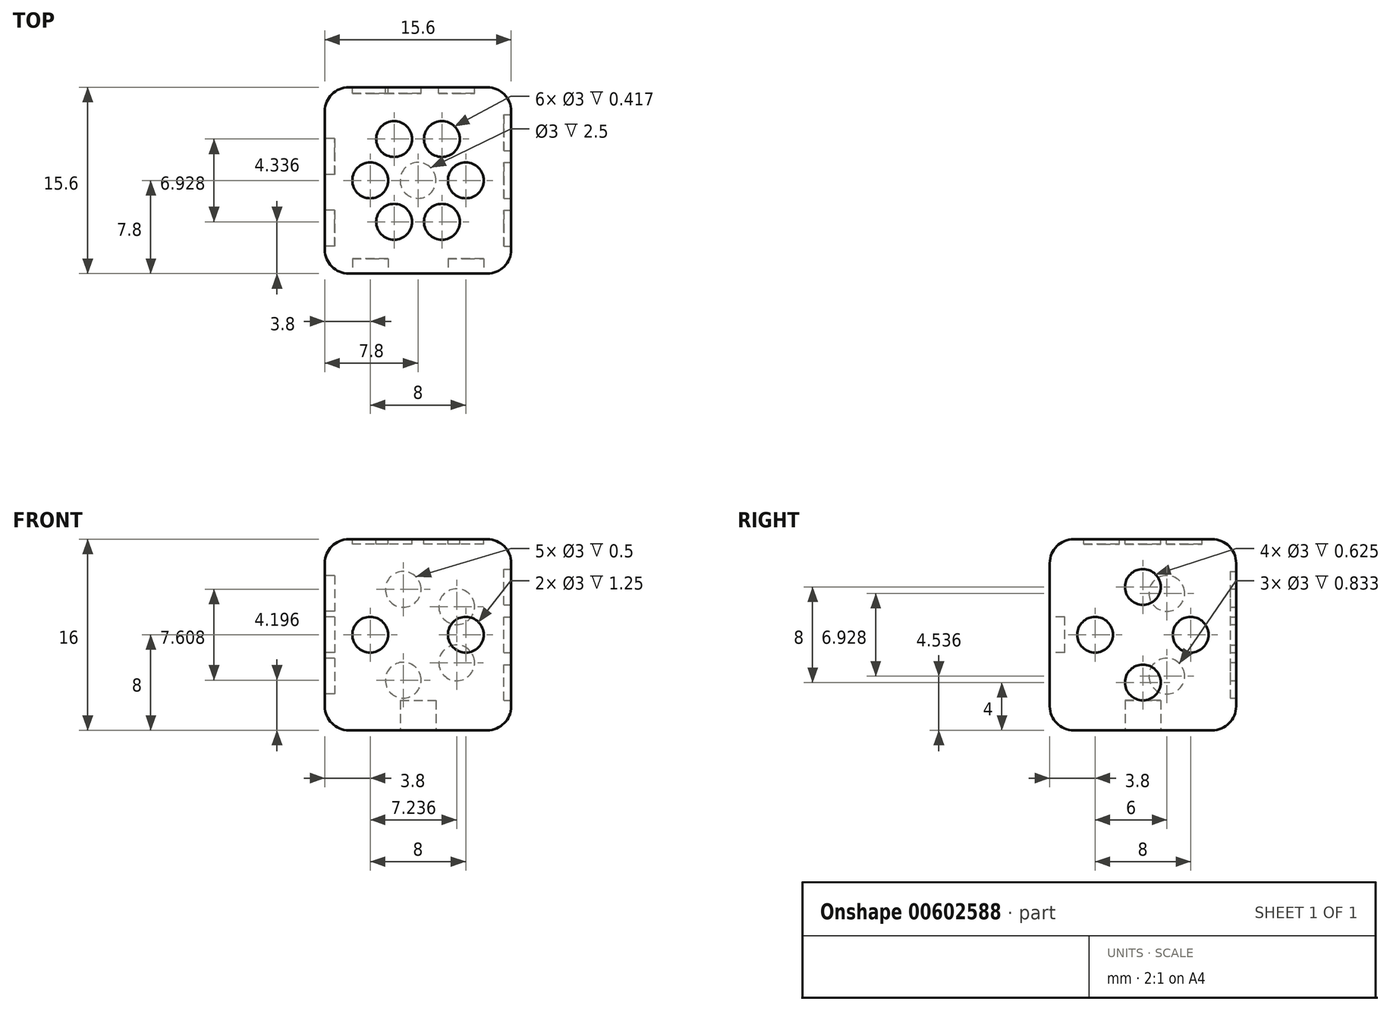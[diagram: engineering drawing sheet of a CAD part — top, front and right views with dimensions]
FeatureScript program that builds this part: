
annotation { "Feature Type Name" : "Feature", "Feature Type Description" : "" }
export const myFeature = defineFeature(function(context is Context, id is Id, definition is map)
    precondition{}
    {
        {
            assignVariable(context, id + "F0", {"name" : "size", "anyValue" : 16});
        }
        {
            assignVariable(context, id + "F1", {"name" : "bevel", "anyValue" : 2});
        }
        {
            assignVariable(context, id + "F2", {"name" : "pip_depth", "anyValue" : 2.5});
        }
        {
            var Q0;
            Q0=qCreatedBy(makeId("Top.planeOp"),FACE);
            var sketch = newSketch(context, id + "F3", { "sketchPlane" : qUnion([Q0])});
            skLineSegment(sketch, "E0.bottom", {"start": v(7.8, -7.8) * mm, "end": v(-7.8, -7.8) * mm});
            skLineSegment(sketch, "E0.top", {"start": v(7.8, 7.8) * mm, "end": v(-7.8, 7.8) * mm});
            skLineSegment(sketch, "E0.left", {"start": v(7.8, -7.8) * mm, "end": v(7.8, 7.8) * mm});
            skLineSegment(sketch, "E0.right", {"start": v(-7.8, -7.8) * mm, "end": v(-7.8, 7.8) * mm});
            skPoint(sketch, "E0.middle", {"position": v(0, 0) * mm});
            skSolve(sketch);
        }
        {
            var Q0;
            Q0=makeQuery(id+"F3.imprint","IMPRINT",FACE,{"disambiguationData":[TD([[makeQuery(id+"F3.imprint","IMPRINT",EDGE,{"derivedFrom":sQuery(id+"F3.wireOp",EDGE,"E0.bottom")}),-1.0]])]});
            extrude(context, id + "F4", {"entities" : qUnion([Q0]), "depth" : (getVariable(context, 'size') / 2) * mm, "offsetDistance" : 25 * mm, "hasSecondDirection" : true, "secondDirectionOppositeDirection" : true, "secondDirectionDepth" : (getVariable(context, 'size') / 2) * mm});
        }
        {
            var Q0;
            Q0=makeQuery(id+"F4.opExtrude","CAP_EDGE",EDGE,{"disambiguationData":[OSD([sQuery(id+"F3.wireOp",EDGE,"E0.bottom")])],"isStart":false});
            var Q1;
            Q1=makeQuery(id+"F4.opExtrude","CAP_EDGE",EDGE,{"disambiguationData":[OSD([sQuery(id+"F3.wireOp",EDGE,"E0.left")])],"isStart":false});
            var Q2;
            Q2=makeQuery(id+"F4.opExtrude","CAP_EDGE",EDGE,{"disambiguationData":[OSD([sQuery(id+"F3.wireOp",EDGE,"E0.top")])],"isStart":false});
            var Q3;
            Q3=makeQuery(id+"F4.opExtrude","CAP_EDGE",EDGE,{"disambiguationData":[OSD([sQuery(id+"F3.wireOp",EDGE,"E0.right")])],"isStart":false});
            var Q4;
            Q4=makeQuery(id+"F4.opExtrude","SWEPT_EDGE",EDGE,{"disambiguationData":[OSD([sQuery(id+"F3.wireOp",EDGE,"E0.top"),sQuery(id+"F3.wireOp",EDGE,"E0.right")])]});
            var Q5;
            Q5=makeQuery(id+"F4.opExtrude","SWEPT_EDGE",EDGE,{"disambiguationData":[OSD([sQuery(id+"F3.wireOp",EDGE,"E0.top"),sQuery(id+"F3.wireOp",EDGE,"E0.left")])]});
            var Q6;
            Q6=makeQuery(id+"F4.opExtrude","CAP_EDGE",EDGE,{"disambiguationData":[OSD([sQuery(id+"F3.wireOp",EDGE,"E0.top")])],"isStart":true});
            var Q7;
            Q7=makeQuery(id+"F4.opExtrude","CAP_EDGE",EDGE,{"disambiguationData":[OSD([sQuery(id+"F3.wireOp",EDGE,"E0.right")])],"isStart":true});
            var Q8;
            Q8=makeQuery(id+"F4.opExtrude","CAP_EDGE",EDGE,{"disambiguationData":[OSD([sQuery(id+"F3.wireOp",EDGE,"E0.left")])],"isStart":true});
            var Q9;
            Q9=makeQuery(id+"F4.opExtrude","SWEPT_EDGE",EDGE,{"disambiguationData":[OSD([sQuery(id+"F3.wireOp",EDGE,"E0.bottom"),sQuery(id+"F3.wireOp",EDGE,"E0.left")])]});
            var Q10;
            Q10=makeQuery(id+"F4.opExtrude","CAP_EDGE",EDGE,{"disambiguationData":[OSD([sQuery(id+"F3.wireOp",EDGE,"E0.bottom")])],"isStart":true});
            var Q11;
            Q11=makeQuery(id+"F4.opExtrude","SWEPT_EDGE",EDGE,{"disambiguationData":[OSD([sQuery(id+"F3.wireOp",EDGE,"E0.bottom"),sQuery(id+"F3.wireOp",EDGE,"E0.right")])]});
            fillet(context, id + "F5", {"entities" : qUnion([Q0, Q1, Q2, Q3, Q4, Q5, Q6, Q7, Q8, Q9, Q10, Q11]), "radius" : (getVariable(context, 'bevel')) * mm, "tangentPropagation" : true, "allowEdgeOverflow" : false});
        }
        {
            var Q0;
            Q0=makeQuery(id+"F4.opExtrude","CAP_FACE",FACE,{"disambiguationData":[OSD([sQuery(id+"F3.wireOp",EDGE,"E0.bottom"),sQuery(id+"F3.wireOp",EDGE,"E0.top"),sQuery(id+"F3.wireOp",EDGE,"E0.left"),sQuery(id+"F3.wireOp",EDGE,"E0.right")])],"isStart":true});
            cPlane(context, id + "F6", {"entities" : qUnion([Q0]), "cplaneType" : CPlaneType.OFFSET, "offset" : 0 * mm, "width" : 150 * mm, "height" : 150 * mm});
        }
        {
            var Q0;
            Q0=qCreatedBy(id+"F6.planeOp",FACE);
            var sketch = newSketch(context, id + "F7", { "sketchPlane" : qUnion([Q0])});
            skCircle(sketch, "E1", {"center": v(0, 0) * mm, "radius": 1.5 * mm});
            skSolve(sketch);
        }
        {
            var Q0;
            Q0=makeQuery(id+"F7.imprint","IMPRINT",FACE,{"disambiguationData":[TD([[makeQuery(id+"F7.imprint","IMPRINT",EDGE,{"derivedFrom":sQuery(id+"F7.wireOp",EDGE,"E1")}),1.0]])]});
            extrude(context, id + "F8", {"entities" : qUnion([Q0]), "operationType" : NewBodyOperationType.REMOVE, "oppositeDirection" : true, "depth" : (getVariable(context, 'pip_depth')) * mm, "offsetDistance" : 25 * mm});
        }
        {
            var Q0;
            Q0=makeQuery(id+"F4.opExtrude","CAP_FACE",FACE,{"disambiguationData":[OSD([sQuery(id+"F3.wireOp",EDGE,"E0.bottom"),sQuery(id+"F3.wireOp",EDGE,"E0.top"),sQuery(id+"F3.wireOp",EDGE,"E0.left"),sQuery(id+"F3.wireOp",EDGE,"E0.right")])],"isStart":false});
            cPlane(context, id + "F9", {"entities" : qUnion([Q0]), "cplaneType" : CPlaneType.OFFSET, "offset" : 0 * mm, "width" : 150 * mm, "height" : 150 * mm});
        }
        {
            var Q0;
            Q0=qCreatedBy(id+"F9.planeOp",FACE);
            var sketch = newSketch(context, id + "F10", { "sketchPlane" : qUnion([Q0])});
            skCircle(sketch, "E2", {"center": v(0, 0) * mm, "radius": 4 * mm, "construction": true});
            skCircle(sketch, "E3", {"center": v(4, 0) * mm, "radius": 1.5 * mm});
            skCircle(sketch, "E4.1.0", {"center": v(2, 3.46) * mm, "radius": 1.5 * mm});
            skCircle(sketch, "E4.2.0", {"center": v(-2, 3.46) * mm, "radius": 1.5 * mm});
            skCircle(sketch, "E5.1.3.0", {"center": v(-4, 0) * mm, "radius": 1.5 * mm});
            skCircle(sketch, "E5.1.4.0", {"center": v(-2, -3.46) * mm, "radius": 1.5 * mm});
            skCircle(sketch, "E5.1.5.0", {"center": v(2, -3.46) * mm, "radius": 1.5 * mm});
            skSolve(sketch);
        }
        {
            var Q0;
            Q0=makeQuery(id+"F10.imprint","IMPRINT",FACE,{"disambiguationData":[TD([[makeQuery(id+"F10.imprint","IMPRINT",EDGE,{"derivedFrom":sQuery(id+"F10.wireOp",EDGE,"E4.2.0")}),1.0]])]});
            var Q1;
            Q1=makeQuery(id+"F10.imprint","IMPRINT",FACE,{"disambiguationData":[TD([[makeQuery(id+"F10.imprint","IMPRINT",EDGE,{"derivedFrom":sQuery(id+"F10.wireOp",EDGE,"E4.1.0")}),1.0]])]});
            var Q2;
            Q2=makeQuery(id+"F10.imprint","IMPRINT",FACE,{"disambiguationData":[TD([[makeQuery(id+"F10.imprint","IMPRINT",EDGE,{"derivedFrom":sQuery(id+"F10.wireOp",EDGE,"E3")}),1.0]])]});
            var Q3;
            Q3=makeQuery(id+"F10.imprint","IMPRINT",FACE,{"disambiguationData":[TD([[makeQuery(id+"F10.imprint","IMPRINT",EDGE,{"derivedFrom":sQuery(id+"F10.wireOp",EDGE,"E5.1.5.0")}),1.0]])]});
            var Q4;
            Q4=makeQuery(id+"F10.imprint","IMPRINT",FACE,{"disambiguationData":[TD([[makeQuery(id+"F10.imprint","IMPRINT",EDGE,{"derivedFrom":sQuery(id+"F10.wireOp",EDGE,"E5.1.4.0")}),1.0]])]});
            var Q5;
            Q5=makeQuery(id+"F10.imprint","IMPRINT",FACE,{"disambiguationData":[TD([[makeQuery(id+"F10.imprint","IMPRINT",EDGE,{"derivedFrom":sQuery(id+"F10.wireOp",EDGE,"E5.1.3.0")}),1.0]])]});
            extrude(context, id + "F11", {"entities" : qUnion([Q0, Q1, Q2, Q3, Q4, Q5]), "operationType" : NewBodyOperationType.REMOVE, "oppositeDirection" : true, "depth" : (getVariable(context, 'pip_depth') / 6) * mm, "offsetDistance" : 25 * mm});
        }
        {
            var Q0;
            Q0=makeQuery(id+"F4.opExtrude","SWEPT_FACE",FACE,{"disambiguationData":[OSD([sQuery(id+"F3.wireOp",EDGE,"E0.bottom")])]});
            cPlane(context, id + "F12", {"entities" : qUnion([Q0]), "cplaneType" : CPlaneType.OFFSET, "offset" : 0 * mm, "width" : 150 * mm, "height" : 150 * mm});
        }
        {
            var Q0;
            Q0=qCreatedBy(id+"F12.planeOp",FACE);
            var sketch = newSketch(context, id + "F13", { "sketchPlane" : qUnion([Q0])});
            skCircle(sketch, "E6", {"center": v(0, 0) * mm, "radius": 4 * mm, "construction": true});
            skCircle(sketch, "E7", {"center": v(4, 0) * mm, "radius": 1.5 * mm});
            skCircle(sketch, "E8.1.0", {"center": v(-4, 0) * mm, "radius": 1.5 * mm});
            skSolve(sketch);
        }
        {
            var Q0;
            Q0=makeQuery(id+"F13.imprint","IMPRINT",FACE,{"disambiguationData":[TD([[makeQuery(id+"F13.imprint","IMPRINT",EDGE,{"derivedFrom":sQuery(id+"F13.wireOp",EDGE,"E8.1.0")}),1.0]])]});
            var Q1;
            Q1=makeQuery(id+"F13.imprint","IMPRINT",FACE,{"disambiguationData":[TD([[makeQuery(id+"F13.imprint","IMPRINT",EDGE,{"derivedFrom":sQuery(id+"F13.wireOp",EDGE,"E7")}),1.0]])]});
            extrude(context, id + "F14", {"entities" : qUnion([Q0, Q1]), "operationType" : NewBodyOperationType.REMOVE, "oppositeDirection" : true, "depth" : (getVariable(context, 'pip_depth') / 2) * mm, "offsetDistance" : 25 * mm});
        }
        {
            var Q0;
            Q0=makeQuery(id+"F4.opExtrude","SWEPT_FACE",FACE,{"disambiguationData":[OSD([sQuery(id+"F3.wireOp",EDGE,"E0.right")])]});
            cPlane(context, id + "F15", {"entities" : qUnion([Q0]), "cplaneType" : CPlaneType.OFFSET, "offset" : 0 * mm, "width" : 150 * mm, "height" : 150 * mm});
        }
        {
            var Q0;
            Q0=qCreatedBy(id+"F15.planeOp",FACE);
            var sketch = newSketch(context, id + "F16", { "sketchPlane" : qUnion([Q0])});
            skCircle(sketch, "E9", {"center": v(0, 0) * mm, "radius": 4 * mm, "construction": true});
            skCircle(sketch, "E10", {"center": v(4, 0) * mm, "radius": 1.5 * mm});
            skCircle(sketch, "E11.1.0", {"center": v(-2, 3.46) * mm, "radius": 1.5 * mm});
            skCircle(sketch, "E11.2.0", {"center": v(-2, -3.46) * mm, "radius": 1.5 * mm});
            skSolve(sketch);
        }
        {
            var Q0;
            Q0=makeQuery(id+"F16.imprint","IMPRINT",FACE,{"disambiguationData":[TD([[makeQuery(id+"F16.imprint","IMPRINT",EDGE,{"derivedFrom":sQuery(id+"F16.wireOp",EDGE,"E11.1.0")}),1.0]])]});
            var Q1;
            Q1=makeQuery(id+"F16.imprint","IMPRINT",FACE,{"disambiguationData":[TD([[makeQuery(id+"F16.imprint","IMPRINT",EDGE,{"derivedFrom":sQuery(id+"F16.wireOp",EDGE,"E11.2.0")}),1.0]])]});
            var Q2;
            Q2=makeQuery(id+"F16.imprint","IMPRINT",FACE,{"disambiguationData":[TD([[makeQuery(id+"F16.imprint","IMPRINT",EDGE,{"derivedFrom":sQuery(id+"F16.wireOp",EDGE,"E10")}),1.0]])]});
            extrude(context, id + "F17", {"entities" : qUnion([Q0, Q1, Q2]), "operationType" : NewBodyOperationType.REMOVE, "oppositeDirection" : true, "depth" : (getVariable(context, 'pip_depth') / 3) * mm, "offsetDistance" : 25 * mm});
        }
        {
            var Q0;
            Q0=makeQuery(id+"F4.opExtrude","SWEPT_FACE",FACE,{"disambiguationData":[OSD([sQuery(id+"F3.wireOp",EDGE,"E0.left")])]});
            cPlane(context, id + "F18", {"entities" : qUnion([Q0]), "cplaneType" : CPlaneType.OFFSET, "offset" : 0 * mm, "width" : 150 * mm, "height" : 150 * mm});
        }
        {
            var Q0;
            Q0=qCreatedBy(id+"F18.planeOp",FACE);
            var sketch = newSketch(context, id + "F19", { "sketchPlane" : qUnion([Q0])});
            skCircle(sketch, "E12", {"center": v(0, 0) * mm, "radius": 4 * mm, "construction": true});
            skCircle(sketch, "E13", {"center": v(4, 0) * mm, "radius": 1.5 * mm});
            skCircle(sketch, "E14.1.0", {"center": v(0, 4) * mm, "radius": 1.5 * mm});
            skCircle(sketch, "E14.2.0", {"center": v(-4, 0) * mm, "radius": 1.5 * mm});
            skCircle(sketch, "E15.1.3.0", {"center": v(0, -4) * mm, "radius": 1.5 * mm});
            skSolve(sketch);
        }
        {
            var Q0;
            Q0=makeQuery(id+"F19.imprint","IMPRINT",FACE,{"disambiguationData":[TD([[makeQuery(id+"F19.imprint","IMPRINT",EDGE,{"derivedFrom":sQuery(id+"F19.wireOp",EDGE,"E14.2.0")}),1.0]])]});
            var Q1;
            Q1=makeQuery(id+"F19.imprint","IMPRINT",FACE,{"disambiguationData":[TD([[makeQuery(id+"F19.imprint","IMPRINT",EDGE,{"derivedFrom":sQuery(id+"F19.wireOp",EDGE,"E14.1.0")}),1.0]])]});
            var Q2;
            Q2=makeQuery(id+"F19.imprint","IMPRINT",FACE,{"disambiguationData":[TD([[makeQuery(id+"F19.imprint","IMPRINT",EDGE,{"derivedFrom":sQuery(id+"F19.wireOp",EDGE,"E13")}),1.0]])]});
            var Q3;
            Q3=makeQuery(id+"F19.imprint","IMPRINT",FACE,{"disambiguationData":[TD([[makeQuery(id+"F19.imprint","IMPRINT",EDGE,{"derivedFrom":sQuery(id+"F19.wireOp",EDGE,"E15.1.3.0")}),1.0]])]});
            extrude(context, id + "F20", {"entities" : qUnion([Q0, Q1, Q2, Q3]), "operationType" : NewBodyOperationType.REMOVE, "oppositeDirection" : true, "depth" : (getVariable(context, 'pip_depth') / 4) * mm, "offsetDistance" : 25 * mm});
        }
        {
            var Q0;
            Q0=makeQuery(id+"F4.opExtrude","SWEPT_FACE",FACE,{"disambiguationData":[OSD([sQuery(id+"F3.wireOp",EDGE,"E0.top")])]});
            cPlane(context, id + "F21", {"entities" : qUnion([Q0]), "cplaneType" : CPlaneType.OFFSET, "offset" : 0 * mm, "width" : 150 * mm, "height" : 150 * mm});
        }
        {
            var Q0;
            Q0=qCreatedBy(id+"F21.planeOp",FACE);
            var sketch = newSketch(context, id + "F22", { "sketchPlane" : qUnion([Q0])});
            skCircle(sketch, "E16", {"center": v(0, 0) * mm, "radius": 4 * mm, "construction": true});
            skCircle(sketch, "E17", {"center": v(4, 0) * mm, "radius": 1.5 * mm});
            skCircle(sketch, "E18.1.0", {"center": v(1.24, 3.8) * mm, "radius": 1.5 * mm});
            skCircle(sketch, "E18.2.0", {"center": v(-3.24, 2.35) * mm, "radius": 1.5 * mm});
            skCircle(sketch, "E19.1.3.0", {"center": v(-3.24, -2.35) * mm, "radius": 1.5 * mm});
            skCircle(sketch, "E19.1.4.0", {"center": v(1.24, -3.8) * mm, "radius": 1.5 * mm});
            skSolve(sketch);
        }
        {
            var Q0;
            Q0=makeQuery(id+"F22.imprint","IMPRINT",FACE,{"disambiguationData":[TD([[makeQuery(id+"F22.imprint","IMPRINT",EDGE,{"derivedFrom":sQuery(id+"F22.wireOp",EDGE,"E18.2.0")}),1.0]])]});
            var Q1;
            Q1=makeQuery(id+"F22.imprint","IMPRINT",FACE,{"disambiguationData":[TD([[makeQuery(id+"F22.imprint","IMPRINT",EDGE,{"derivedFrom":sQuery(id+"F22.wireOp",EDGE,"E18.1.0")}),1.0]])]});
            var Q2;
            Q2=makeQuery(id+"F22.imprint","IMPRINT",FACE,{"disambiguationData":[TD([[makeQuery(id+"F22.imprint","IMPRINT",EDGE,{"derivedFrom":sQuery(id+"F22.wireOp",EDGE,"E17")}),1.0]])]});
            var Q3;
            Q3=makeQuery(id+"F22.imprint","IMPRINT",FACE,{"disambiguationData":[TD([[makeQuery(id+"F22.imprint","IMPRINT",EDGE,{"derivedFrom":sQuery(id+"F22.wireOp",EDGE,"E19.1.4.0")}),1.0]])]});
            var Q4;
            Q4=makeQuery(id+"F22.imprint","IMPRINT",FACE,{"disambiguationData":[TD([[makeQuery(id+"F22.imprint","IMPRINT",EDGE,{"derivedFrom":sQuery(id+"F22.wireOp",EDGE,"E19.1.3.0")}),1.0]])]});
            extrude(context, id + "F23", {"entities" : qUnion([Q0, Q1, Q2, Q3, Q4]), "operationType" : NewBodyOperationType.REMOVE, "oppositeDirection" : true, "depth" : (getVariable(context, 'pip_depth') / 5) * mm, "offsetDistance" : 25 * mm});
        }
    });
